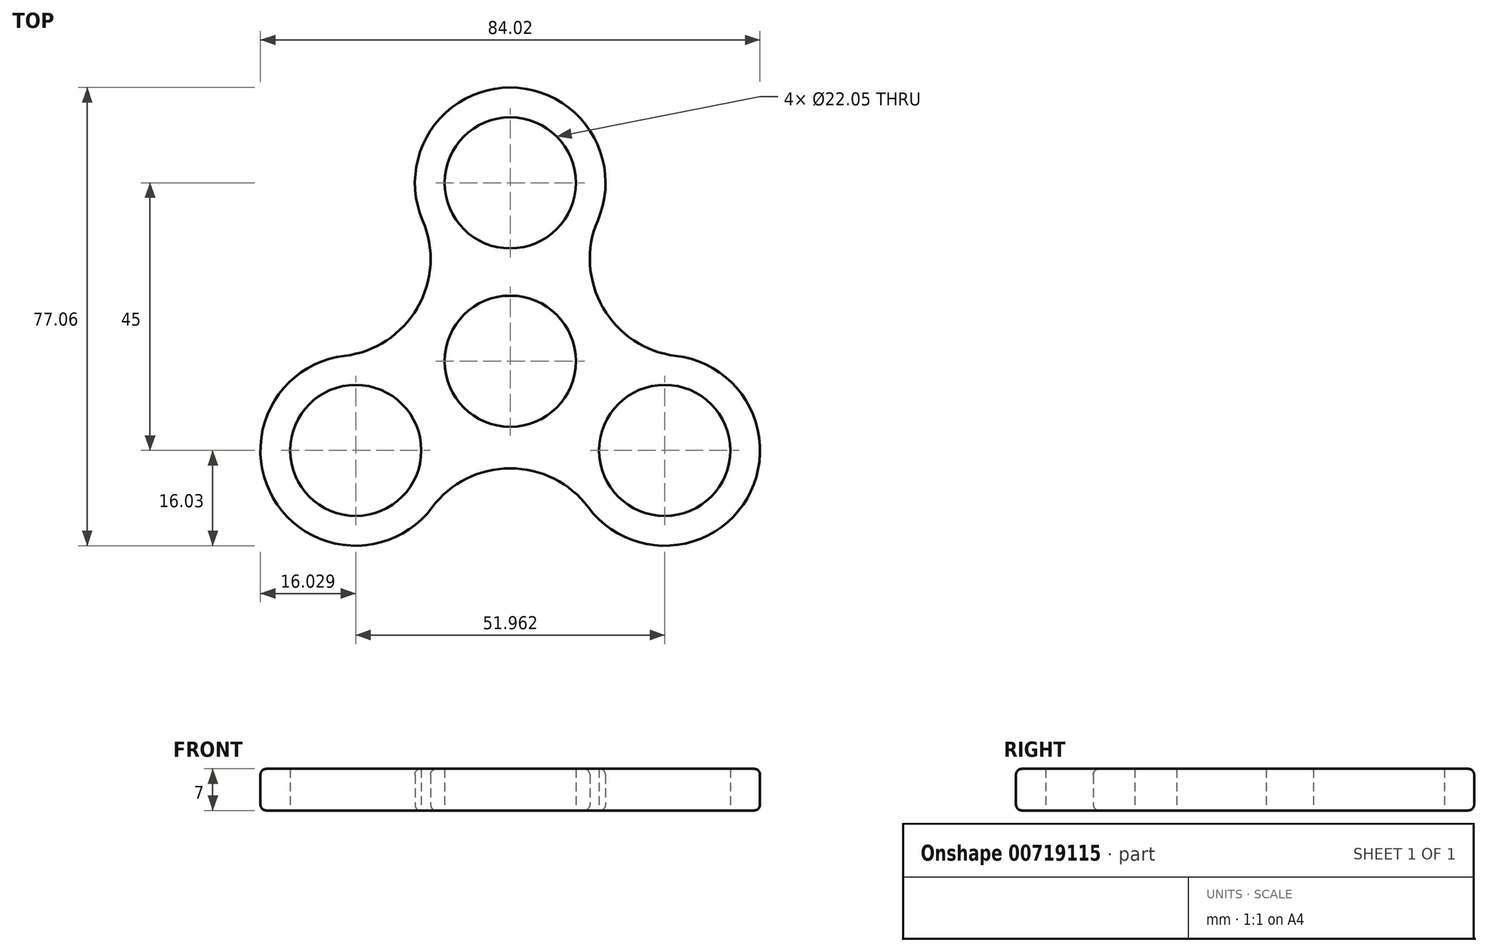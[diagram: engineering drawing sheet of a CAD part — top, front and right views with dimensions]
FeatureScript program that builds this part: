
annotation { "Feature Type Name" : "Feature", "Feature Type Description" : "" }
export const myFeature = defineFeature(function(context is Context, id is Id, definition is map)
    precondition{}
    {
        {
            var Q0;
            Q0=qCreatedBy(makeId("Top.planeOp"),FACE);
            var sketch = newSketch(context, id + "F0", { "sketchPlane" : qUnion([Q0])});
            skCircle(sketch, "E0", {"center": v(0, 0) * mm, "radius": 11.03 * mm});
            skCircle(sketch, "E1", {"center": v(0, 30) * mm, "radius": 11.03 * mm});
            skCircle(sketch, "E2.0", {"center": v(0, 30) * mm, "radius": 16.02 * mm});
            skCircle(sketch, "E3.0", {"center": v(0, 0) * mm, "radius": 18.02 * mm});
            skArc(sketch, "E4", {"start": v(-15.59, 9.05) * mm, "mid": v(-13.42, 16.25) * mm, "end": v(-14.72, 23.66) * mm});
            skLineSegment(sketch, "E5", {"start": v(0, -22.67) * mm, "end": v(0, 73.3) * mm, "construction": true});
            skArc(sketch, "E6.MirrorCS", {"start": v(15.59, 9.05) * mm, "mid": v(13.42, 16.25) * mm, "end": v(14.72, 23.66) * mm});
            skArc(sketch, "E7.1.0", {"start": v(-0.04, -18.02) * mm, "mid": v(-7.36, -19.75) * mm, "end": v(-13.13, -24.58) * mm});
            skArc(sketch, "E7.1.1", {"start": v(-15.63, 8.98) * mm, "mid": v(-20.78, 3.5) * mm, "end": v(-27.85, 0.92) * mm});
            skCircle(sketch, "E7.1.2", {"center": v(-25.98, -15) * mm, "radius": 16.02 * mm});
            skCircle(sketch, "E7.1.3", {"center": v(-25.98, -15) * mm, "radius": 11.03 * mm});
            skArc(sketch, "E7.2.0", {"start": v(15.63, 8.98) * mm, "mid": v(20.78, 3.5) * mm, "end": v(27.85, 0.92) * mm});
            skArc(sketch, "E7.2.1", {"start": v(0.04, -18.02) * mm, "mid": v(7.36, -19.75) * mm, "end": v(13.13, -24.58) * mm});
            skCircle(sketch, "E7.2.2", {"center": v(25.98, -15) * mm, "radius": 16.02 * mm});
            skCircle(sketch, "E7.2.3", {"center": v(25.98, -15) * mm, "radius": 11.03 * mm});
            skSolve(sketch);
        }
        {
            var Q0;
            Q0=qSketchRegion(id+"F0",true);
            var Q1;
            Q1=makeQuery(id+"F0.imprint","IMPRINT",FACE,{"disambiguationData":[TD([[makeQuery(id+"F0.imprint","IMPRINT",EDGE,{"derivedFrom":sQuery(id+"F0.wireOp",EDGE,"E0")}),-1.0]])]});
            var Q2;
            {var subQ0=sQuery(id+"F0.wireOp",EDGE,"E7.1.2");var subQ1=sQuery(id+"F0.wireOp",EDGE,"E3.0");var subQ2=makeQuery(id+"F0.imprint","INTERSECT",VERTEX,{"disambiguationData":[OD(0.0)],"derivedFrom":[subQ1,subQ0]});Q2=makeQuery(id+"F0.imprint","IMPRINT",FACE,{"disambiguationData":[TD([[makeQuery(id+"F0.imprint","IMPRINT",EDGE,{"disambiguationData":[TD([[subQ2,-1.0]])],"derivedFrom":subQ1}),1.0]])]});}
            var Q3;
            {var subQ0=sQuery(id+"F0.wireOp",EDGE,"E3.0");var subQ1=sQuery(id+"F0.wireOp",EDGE,"E2.0");var subQ2=makeQuery(id+"F0.imprint","INTERSECT",VERTEX,{"disambiguationData":[OD(0.0)],"derivedFrom":[subQ1,subQ0]});Q3=makeQuery(id+"F0.imprint","IMPRINT",FACE,{"disambiguationData":[TD([[makeQuery(id+"F0.imprint","IMPRINT",EDGE,{"disambiguationData":[TD([[subQ2,-1.0]])],"derivedFrom":subQ1}),1.0]])]});}
            var Q4;
            {var subQ0=sQuery(id+"F0.wireOp",EDGE,"E7.2.2");var subQ1=sQuery(id+"F0.wireOp",EDGE,"E3.0");var subQ2=makeQuery(id+"F0.imprint","INTERSECT",VERTEX,{"disambiguationData":[OD(0.0)],"derivedFrom":[subQ1,subQ0]});Q4=makeQuery(id+"F0.imprint","IMPRINT",FACE,{"disambiguationData":[TD([[makeQuery(id+"F0.imprint","IMPRINT",EDGE,{"disambiguationData":[TD([[subQ2,-1.0]])],"derivedFrom":subQ1}),1.0]])]});}
            extrude(context, id + "F1", {"entities" : qUnion([Q0, Q1, Q2, Q3, Q4]), "depth" : 7 * mm, "offsetDistance" : 25 * mm});
        }
        {
            var Q0;
            Q0=makeQuery(id+"F1.opExtrude","SWEPT_FACE",FACE,{"disambiguationData":[OSD([sQuery(id+"F0.wireOp",EDGE,"E2.0")])]});
            var Q1;
            Q1=makeQuery(id+"F1.opExtrude","SWEPT_FACE",FACE,{"disambiguationData":[OSD([sQuery(id+"F0.wireOp",EDGE,"E4")])]});
            var Q2;
            Q2=makeQuery(id+"F1.opExtrude","SWEPT_FACE",FACE,{"disambiguationData":[OSD([sQuery(id+"F0.wireOp",EDGE,"E7.1.1")])]});
            var Q3;
            Q3=makeQuery(id+"F1.opExtrude","SWEPT_FACE",FACE,{"disambiguationData":[OSD([sQuery(id+"F0.wireOp",EDGE,"E7.1.2")])]});
            var Q4;
            Q4=makeQuery(id+"F1.opExtrude","SWEPT_FACE",FACE,{"disambiguationData":[OSD([sQuery(id+"F0.wireOp",EDGE,"E7.2.1")])]});
            fillet(context, id + "F2", {"entities" : qUnion([Q0, Q1, Q2, Q3, Q4]), "radius" : 1 * mm, "tangentPropagation" : true, "allowEdgeOverflow" : false});
        }
    });
